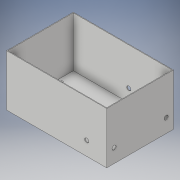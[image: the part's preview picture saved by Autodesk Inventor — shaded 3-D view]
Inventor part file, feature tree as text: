
AUTODESK INVENTOR PART (.ipt)
format: ipt  version: 2018 (Build 220112000, 112)  size: 179,712 bytes
history: native  units: in
note: dims shown in document units (in); Inventor stores cm internally (conversion verified against a paired STEP export)
features: extrude x7, sketch x7
ambient origin geometry x8: Origin, YZ Plane, XZ Plane, XY Plane, X Axis, Y Axis, Z Axis, Center Point
bodies: Solid1 (feature_tree)
feature tree (14):
  extrude  "Extrusion1"  Depth=4.0in
  extrude  "Extrusion2"  Depth=5.92in
  extrude  "Extrusion3"  Depth=3.0in TaperAngle=0.0deg
  sketch  "Sketch4"  dims[d10=0.164in d11=0.164in]
  extrude  "Extrusion5"  Depth=0.164in
  extrude  "Extrusion6"  Depth=2.598in
  extrude  "Extrusion7"  Depth=0.118in
  extrude  "Extrusion8"  Depth=0.118in
  sketch  "Sketch1"  dims[d0=6.0in d1=4.0in]
  sketch  "Sketch2"  dims[d2=0.08in d3=0.0in d4=5.92in]
  sketch  "Sketch3"  dims[d5=3.92in d6=3.0in d7=0.0in]
  sketch  "Sketch5"  dims[d12=0.0in d13=0.0in d14=2.598in]
  sketch  "Sketch6"  dims[d15=0.787in d16=0.118in]
  sketch  "Sketch7"  dims[d17=0.118in d18=0.118in d19=0.118in d21=2.1875in d39=0.25in d40=0.25in d41=0.25in d42=0.0in d43=0.0in d44=0.25in d45=0.25in d46=0.0in d47=0.0in d51=0.25in d52=1.0in d53=0.0in d62=5.5625in d63=2.1875in d96=0.12in d97=0.12in d98=0.12in d99=0.12in d103=0.12in d106=0.12in d111=0.12in d112=0.12in d113=0.12in d114=0.0in d115=0.0in]
